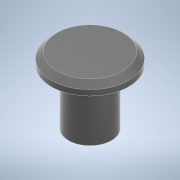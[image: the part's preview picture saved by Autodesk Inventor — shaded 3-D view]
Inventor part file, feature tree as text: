
AUTODESK INVENTOR PART (.ipt)
format: ipt  version: 2021 (Build 250183000, 183)  size: 244,736 bytes
history: native  units: mm
features: extrude x2, sketch x2, chamfer x1
ambient origin geometry x8: Origin, YZ Plane, XZ Plane, XY Plane, X Axis, Y Axis, Z Axis, Center Point
bodies: Solid1 (feature_tree)
feature tree (5):
  extrude  "Extrusion1"  Depth=10.0mm TaperAngle=0.0deg
  extrude  "Extrusion2"  Depth=2.0mm TaperAngle=0.0deg
  chamfer  "Chamfer1"  Distance=2.0mm Angle=45.0deg
  sketch  "Sketch1"  dims[d0=7.8mm d1=10.0mm d2=0.0mm]
  sketch  "Sketch2"  dims[d3=14.0mm d4=2.0mm d5=0.0mm d6=1.0mm d7=2.0mm d8=45.0deg]
